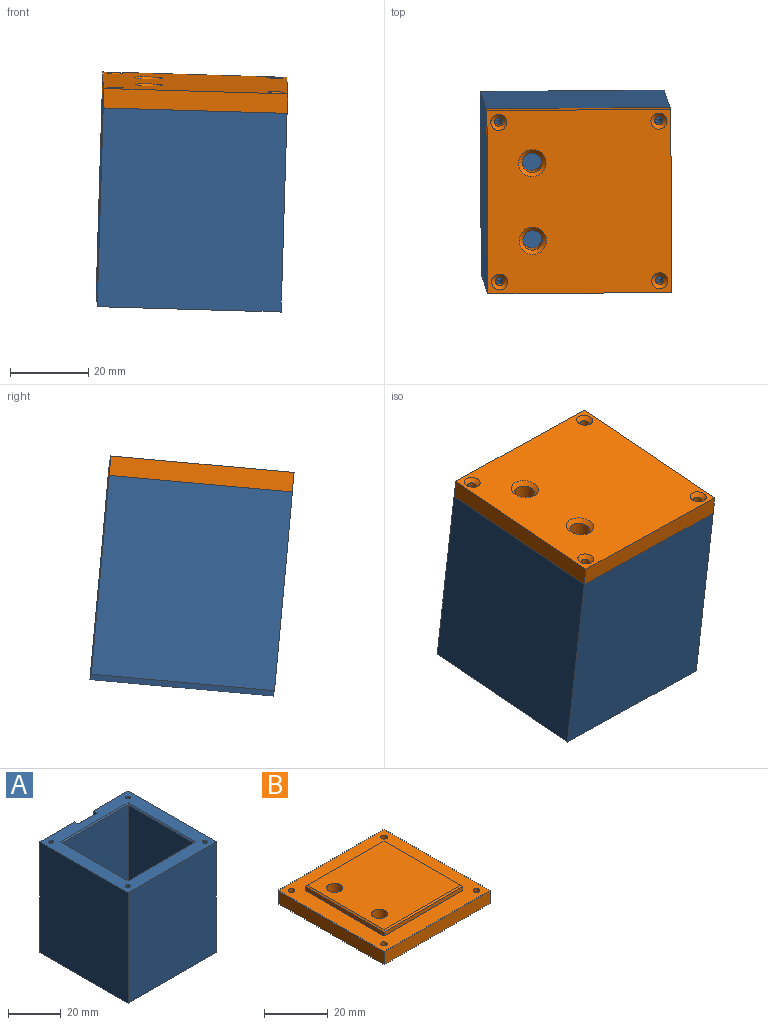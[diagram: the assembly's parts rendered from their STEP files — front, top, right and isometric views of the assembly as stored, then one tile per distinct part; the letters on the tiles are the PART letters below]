
ASSEMBLY  parts=2 mates=1
PART A: 27 faces, bbox 47x47x51 mm
  f0: plane 51x47mm, normal (0,1,0), area 2377mm2, adj f1,f2,f4,f5,f11,f13,f14
  f1: plane 47x47mm, normal (0,0,1), area 881.7mm2, adj f0,f2,f3,f4,f11,f12,f13,f15
  f2: plane 51x47mm, normal (-1,0,0), area 2397mm2, adj f0,f1,f3,f5
  f3: plane 51x47mm, normal (0,-1,0), area 2397mm2, adj f1,f2,f4,f5
  f4: plane 51x47mm, normal (1,0,0), area 2397mm2, adj f0,f1,f3,f5
  f5: plane 47x47mm, normal (0,0,-1), area 2209mm2, adj f0,f2,f3,f4
  f6: plane 49.5x35mm, normal (0,-1,0), area 1732.5mm2, adj f7,f9,f10,f24
  f7: plane 49.5x35mm, normal (1,0,0), area 1732.5mm2, adj f6,f8,f10,f23
  f8: plane 49.5x35mm, normal (0,1,0), area 1732.5mm2, adj f7,f9,f10,f25
  f9: plane 49.5x35mm, normal (-1,0,0), area 1732.5mm2, adj f6,f8,f10,f26
  f10: plane 35x35mm, normal (0,0,1), area 1225mm2, adj f6,f7,f8,f9
  f11: plane 2x2mm, normal (1,0,0), area 4mm2, adj f0,f1,f12,f14
  f12: plane 10x2mm, normal (0,1,0), area 20mm2, adj f1,f11,f13,f14
  f13: plane 2x2mm, normal (-1,0,0), area 4mm2, adj f0,f1,f12,f14
  f14: plane 10x2mm, normal (0,0,1), area 20mm2, adj f0,f11,f12,f13
  f15: cylinder r=0.95mm len=10mm, axis (0,0,1), area 59.7mm2, adj f1,f16
  f16: plane 1.9x1.9mm, normal (0,0,1), area 2.8mm2, adj f15
  f17: cylinder r=0.95mm len=10mm, axis (0,0,1), area 59.7mm2, adj f1,f18
  f18: plane 1.9x1.9mm, normal (0,0,1), area 2.8mm2, adj f17
  f19: cylinder r=0.95mm len=10mm, axis (0,0,1), area 59.7mm2, adj f1,f20
  f20: plane 1.9x1.9mm, normal (0,0,1), area 2.8mm2, adj f19
  f21: cylinder r=0.95mm len=10mm, axis (0,0,1), area 59.7mm2, adj f1,f22
  f22: plane 1.9x1.9mm, normal (0,0,1), area 2.8mm2, adj f21
  f23: plane 36x0.5mm, normal (0.71,0,0.71), area 25.1mm2, adj f1,f7,f24,f25
  f24: plane 36x0.5mm, normal (0,-0.71,0.71), area 25.1mm2, adj f1,f6,f23,f26
  f25: plane 36x0.5mm, normal (0,0.71,0.71), area 25.1mm2, adj f1,f8,f23,f26
  f26: plane 36x0.5mm, normal (-0.71,0,0.71), area 25.1mm2, adj f1,f9,f24,f25
PART B: 27 faces, bbox 47x47x7 mm
  f0: plane 47x47mm, normal (0,0,1), area 977.1mm2, adj f1,f2,f3,f4,f6,f7,f8,f9
  f1: plane 47x5mm, normal (-1,0,0), area 235mm2, adj f0,f2,f4,f5
  f2: plane 47x5mm, normal (0,-1,0), area 235mm2, adj f0,f1,f3,f5
  f3: plane 47x5mm, normal (1,0,0), area 235mm2, adj f0,f2,f4,f5
  f4: plane 47x5mm, normal (0,1,0), area 235mm2, adj f0,f1,f3,f5
  f5: plane 47x47mm, normal (0,0,-1), area 2079.2mm2, adj f1,f2,f3,f4,f21,f22,f23,f24
  f6: plane 34.9x1.5mm, normal (0,1,0), area 52.3mm2, adj f0,f7,f9,f17
  f7: plane 34.9x1.5mm, normal (-1,0,0), area 52.3mm2, adj f0,f6,f8,f18
  f8: plane 34.9x1.5mm, normal (0,-1,0), area 52.3mm2, adj f0,f7,f9,f20
  f9: plane 34.9x1.5mm, normal (1,0,0), area 52.3mm2, adj f0,f6,f8,f19
  f10: plane 33.9x33.9mm, normal (0,0,1), area 1109.9mm2, adj f11,f12,f17,f18,f19,f20
  f11: cylinder r=2.5mm len=6mm, axis (0,0,1), area 94.2mm2, adj f10,f22
  f12: cylinder r=2.5mm len=6mm, axis (0,0,1), area 94.2mm2, adj f10,f21
  f13: cylinder r=1.05mm len=4mm, axis (0,0,1), area 26.4mm2, adj f0,f26
  f14: cylinder r=1.05mm len=4mm, axis (0,0,1), area 26.4mm2, adj f0,f25
  f15: cylinder r=1.05mm len=4mm, axis (0,0,1), area 26.4mm2, adj f0,f24
  f16: cylinder r=1.05mm len=4mm, axis (0,0,1), area 26.4mm2, adj f0,f23
  f17: plane 34.9x0.5mm, normal (0,0.71,0.71), area 24.3mm2, adj f6,f10,f18,f19
  f18: plane 34.9x0.5mm, normal (-0.71,0,0.71), area 24.3mm2, adj f7,f10,f17,f20
  f19: plane 34.9x0.5mm, normal (0.71,0,0.71), area 24.3mm2, adj f9,f10,f17,f20
  f20: plane 34.9x0.5mm, normal (0,-0.71,0.71), area 24.3mm2, adj f8,f10,f18,f19
  f21: cone r=3.5mm half-angle=45deg, axis (0,0,-1), area 26.7mm2, adj f5,f12
  f22: cone r=3.5mm half-angle=45deg, axis (0,0,-1), area 26.7mm2, adj f5,f11
  f23: cone r=2.05mm half-angle=45deg, axis (0,0,-1), area 13.8mm2, adj f5,f16
  f24: cone r=2.05mm half-angle=45deg, axis (0,0,-1), area 13.8mm2, adj f5,f15
  f25: cone r=2.05mm half-angle=45deg, axis (0,0,-1), area 13.8mm2, adj f5,f14
  f26: cone r=2.05mm half-angle=45deg, axis (0,0,-1), area 13.8mm2, adj f5,f13
PLACE A rot(axis=(0.03,0.06,-1),89.8deg) t=(-22.4,33.24,-24.06)mm
PLACE B rot(axis=(-1,0,0.01),174.8deg) t=(-20.7,28.25,31.69)mm
MATE fastened B.f16 <-> A.f15  axis (-0.03,0.09,-1) through (23.12,26.03,25.16)mm
